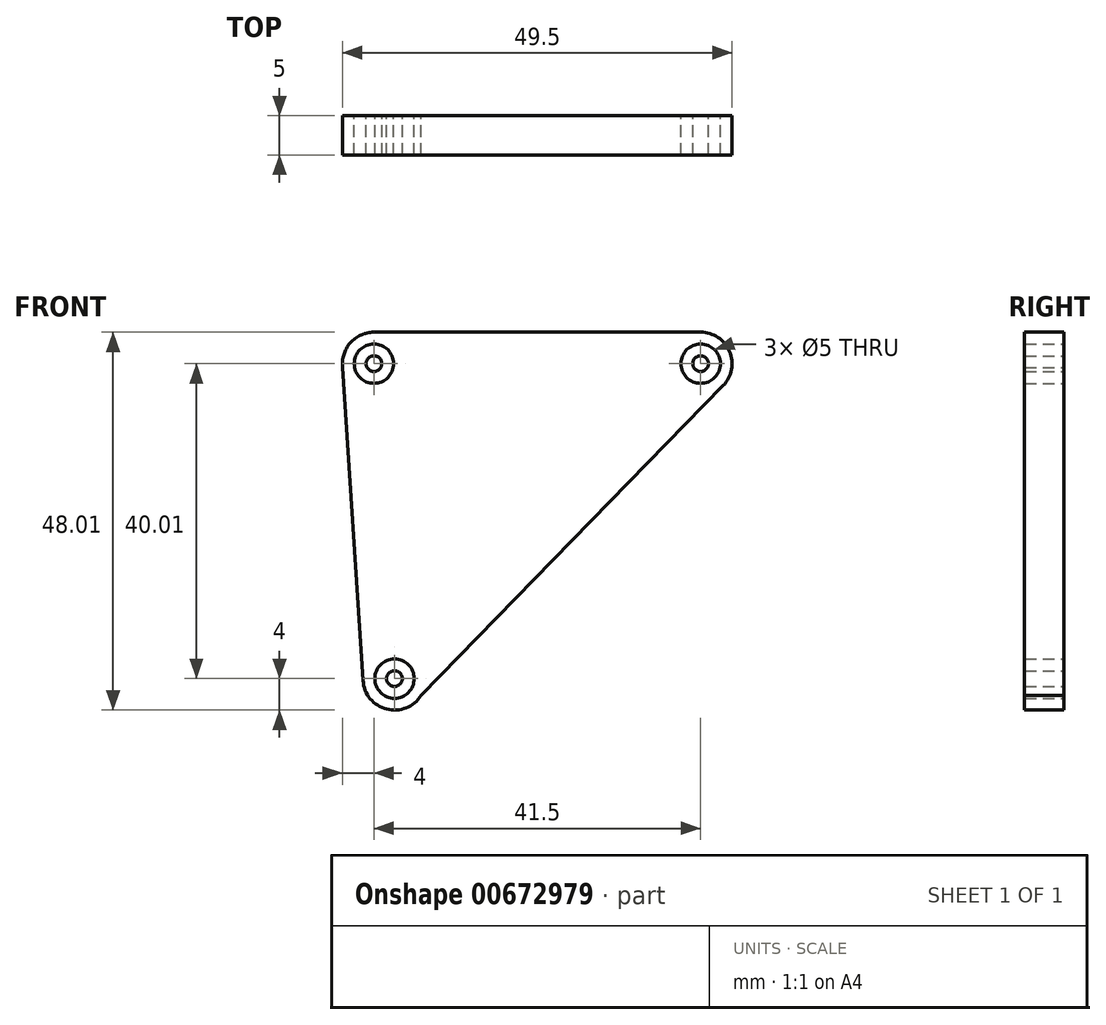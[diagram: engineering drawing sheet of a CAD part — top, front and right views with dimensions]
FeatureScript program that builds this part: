
annotation { "Feature Type Name" : "Feature", "Feature Type Description" : "" }
export const myFeature = defineFeature(function(context is Context, id is Id, definition is map)
    precondition{}
    {
        {
            var Q0;
            Q0=qCreatedBy(makeId("Front.planeOp"),FACE);
            var sketch = newSketch(context, id + "F0", { "sketchPlane" : qUnion([Q0])});
            skArc(sketch, "E0", {"start": v(28.65, -0.05) * mm, "mid": v(29.48, 4.3) * mm, "end": v(25.79, 6.74) * mm});
            skArc(sketch, "E1", {"start": v(-17.1, -37.53) * mm, "mid": v(-14.08, -41.15) * mm, "end": v(-9.72, -39.4) * mm});
            skArc(sketch, "E2", {"start": v(-15.71, 6.74) * mm, "mid": v(-18.72, 5.38) * mm, "end": v(-19.68, 2.22) * mm});
            skLineSegment(sketch, "E3", {"start": v(-19.71, 2.74) * mm, "end": v(-17.1, -37.53) * mm});
            skLineSegment(sketch, "E4", {"start": v(-15.71, 6.74) * mm, "end": v(25.79, 6.74) * mm});
            skLineSegment(sketch, "E5", {"start": v(-9.72, -39.4) * mm, "end": v(28.7, 0) * mm});
            skCircle(sketch, "E6", {"center": v(-15.71, 2.74) * mm, "radius": 2.5 * mm});
            skCircle(sketch, "E7", {"center": v(25.79, 2.74) * mm, "radius": 2.5 * mm});
            skCircle(sketch, "E8", {"center": v(-13.1, -37.27) * mm, "radius": 2.5 * mm});
            skCircle(sketch, "E9", {"center": v(-15.71, 2.74) * mm, "radius": 1 * mm});
            skCircle(sketch, "E10", {"center": v(25.79, 2.74) * mm, "radius": 1 * mm});
            skCircle(sketch, "E11", {"center": v(-13.1, -37.27) * mm, "radius": 1 * mm});
            skSolve(sketch);
        }
        {
            var Q0;
            Q0 = qSketchRegion(id + "F0", true);
            var Q1;
            Q1=makeQuery(id+"F0.imprint","IMPRINT",FACE,{"disambiguationData":[TD([[makeQuery(id+"F0.imprint","IMPRINT",EDGE,{"derivedFrom":sQuery(id+"F0.wireOp",EDGE,"E9")}),1.0]])]});
            var Q2;
            Q2=makeQuery(id+"F0.imprint","IMPRINT",FACE,{"disambiguationData":[TD([[makeQuery(id+"F0.imprint","IMPRINT",EDGE,{"derivedFrom":sQuery(id+"F0.wireOp",EDGE,"E10")}),1.0]])]});
            var Q3;
            Q3=makeQuery(id+"F0.imprint","IMPRINT",FACE,{"disambiguationData":[TD([[makeQuery(id+"F0.imprint","IMPRINT",EDGE,{"derivedFrom":sQuery(id+"F0.wireOp",EDGE,"E11")}),1.0]])]});
            extrude(context, id + "F1", {"entities" : qUnion([Q0, Q1, Q2, Q3]), "depth" : 5 * mm, "offsetDistance" : 25 * mm});
        }
    });
